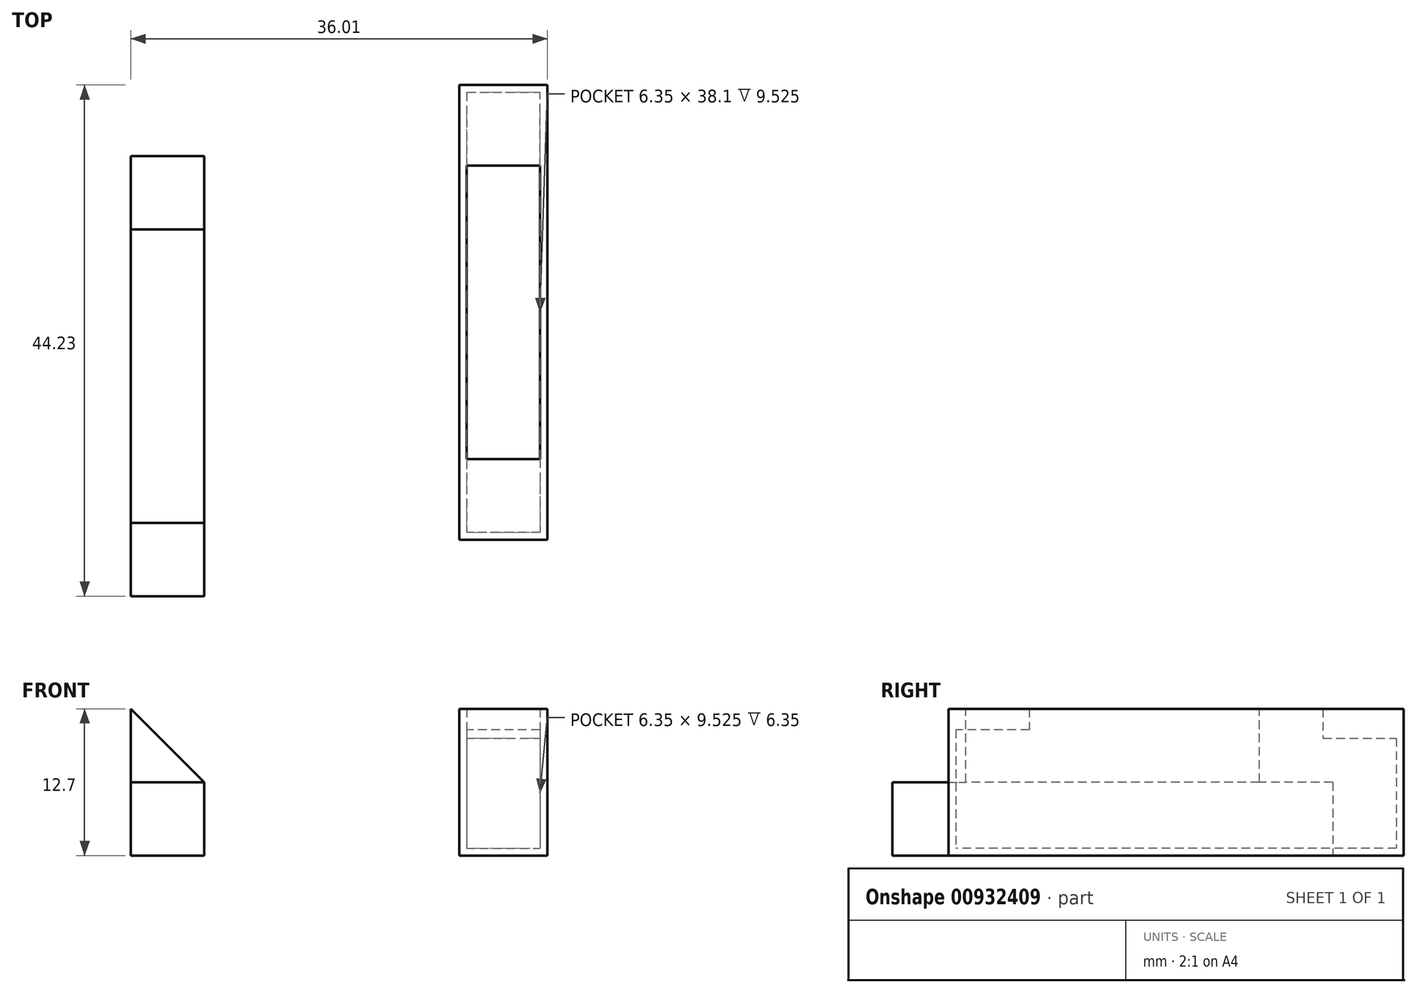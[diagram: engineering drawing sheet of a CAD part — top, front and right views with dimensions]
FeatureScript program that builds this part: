
annotation { "Feature Type Name" : "Feature", "Feature Type Description" : "" }
export const myFeature = defineFeature(function(context is Context, id is Id, definition is map)
    precondition{}
    {
        {
            var Q0;
            Q0=qCreatedBy(makeId("Top.planeOp"),FACE);
            var sketch = newSketch(context, id + "F0", { "sketchPlane" : qUnion([Q0])});
            skLineSegment(sketch, "E0.bottom", {"start": v(0, 0) * mm, "end": v(6.35, 0) * mm});
            skLineSegment(sketch, "E0.top", {"start": v(0, -25.4) * mm, "end": v(6.35, -25.4) * mm});
            skLineSegment(sketch, "E0.left", {"start": v(0, 0) * mm, "end": v(0, -25.4) * mm});
            skLineSegment(sketch, "E0.right", {"start": v(6.35, 0) * mm, "end": v(6.35, -25.4) * mm});
            skLineSegment(sketch, "E1.bottom", {"start": v(28.4, 12.48) * mm, "end": v(36.01, 12.48) * mm});
            skLineSegment(sketch, "E1.top", {"start": v(28.4, -26.89) * mm, "end": v(36.01, -26.89) * mm});
            skLineSegment(sketch, "E1.left", {"start": v(28.4, 12.48) * mm, "end": v(28.4, -26.89) * mm});
            skLineSegment(sketch, "E1.right", {"start": v(36.01, 12.48) * mm, "end": v(36.01, -26.89) * mm});
            skLineSegment(sketch, "E2.bottom", {"start": v(-49.7, 10.3) * mm, "end": v(-42.72, 10.3) * mm});
            skLineSegment(sketch, "E2.top", {"start": v(-49.7, -27.8) * mm, "end": v(-42.72, -27.8) * mm});
            skLineSegment(sketch, "E2.left", {"start": v(-49.7, 10.3) * mm, "end": v(-49.7, -27.8) * mm});
            skLineSegment(sketch, "E2.right", {"start": v(-42.72, 10.3) * mm, "end": v(-42.72, -27.8) * mm});
            skSolve(sketch);
        }
        {
            var Q0;
            Q0=makeQuery(id+"F0.imprint","IMPRINT",FACE,{"disambiguationData":[TD([[makeQuery(id+"F0.imprint","IMPRINT",EDGE,{"derivedFrom":sQuery(id+"F0.wireOp",EDGE,"E0.bottom")}),-1.0]])]});
            extrude(context, id + "F1", {"entities" : qUnion([Q0]), "depth" : 12.7 * mm, "offsetDistance" : 25 * mm});
        }
        {
            var Q0;
            Q0=makeQuery(id+"F1.opExtrude","SWEPT_FACE",FACE,{"disambiguationData":[OSD([sQuery(id+"F0.wireOp",EDGE,"E0.top")])]});
            var sketch = newSketch(context, id + "F2", { "sketchPlane" : qUnion([Q0])});
            skLineSegment(sketch, "E3", {"start": v(6.35, 6.35) * mm, "end": v(0, 12.7) * mm});
            skLineSegment(sketch, "E4", {"start": v(0, 12.7) * mm, "end": v(6.35, 12.7) * mm});
            skLineSegment(sketch, "E5", {"start": v(6.35, 12.7) * mm, "end": v(6.35, 6.35) * mm});
            skSolve(sketch);
        }
        {
            var Q0;
            Q0=makeQuery(id+"F2.imprint","IMPRINT",FACE,{"disambiguationData":[TD([[makeQuery(id+"F2.imprint","IMPRINT",EDGE,{"derivedFrom":sQuery(id+"F2.wireOp",EDGE,"E3")}),-1.0]])]});
            extrude(context, id + "F3", {"entities" : qUnion([Q0]), "operationType" : NewBodyOperationType.REMOVE, "endBound" : BoundingType.UP_TO_NEXT, "oppositeDirection" : true, "depth" : 25.4 * mm, "offsetDistance" : 25.4 * mm});
        }
        {
            var Q0;
            Q0=makeQuery(id+"F0.imprint","IMPRINT",FACE,{"disambiguationData":[TD([[makeQuery(id+"F0.imprint","IMPRINT",EDGE,{"derivedFrom":sQuery(id+"F0.wireOp",EDGE,"E1.bottom")}),-1.0]])]});
            extrude(context, id + "F4", {"entities" : qUnion([Q0]), "depth" : 12.7 * mm, "offsetDistance" : 25.4 * mm});
        }
        {
            var Q0;
            Q0=makeQuery(id+"F4.opExtrude","CAP_FACE",FACE,{"disambiguationData":[OSD([sQuery(id+"F0.wireOp",EDGE,"E1.bottom"),sQuery(id+"F0.wireOp",EDGE,"E1.top"),sQuery(id+"F0.wireOp",EDGE,"E1.left"),sQuery(id+"F0.wireOp",EDGE,"E1.right")])],"isStart":false});
            shell(context, id + "F5", {"entities" : qUnion([Q0]), "thickness" : 0.64 * mm});
        }
        {
            var Q0;
            Q0=makeQuery(id+"F1.opExtrude","SWEPT_FACE",FACE,{"disambiguationData":[OSD([sQuery(id+"F0.wireOp",EDGE,"E0.top")])]});
            var sketch = newSketch(context, id + "F6", { "sketchPlane" : qUnion([Q0])});
            skLineSegment(sketch, "E6", {"start": v(6.35, 6.35) * mm, "end": v(0, 6.35) * mm});
            skLineSegment(sketch, "E7", {"start": v(0, 6.35) * mm, "end": v(0, 0) * mm});
            skLineSegment(sketch, "E8", {"start": v(0, 0) * mm, "end": v(6.35, 0) * mm});
            skLineSegment(sketch, "E9", {"start": v(6.35, 0) * mm, "end": v(6.35, 6.35) * mm});
            skSolve(sketch);
        }
        {
            var Q0;
            Q0=makeQuery(id+"F6.imprint","IMPRINT",FACE,{"disambiguationData":[TD([[makeQuery(id+"F6.imprint","IMPRINT",EDGE,{"derivedFrom":sQuery(id+"F6.wireOp",EDGE,"E6")}),1.0]])]});
            extrude(context, id + "F7", {"entities" : qUnion([Q0]), "operationType" : NewBodyOperationType.ADD, "depth" : 6.35 * mm, "offsetDistance" : 25.4 * mm});
        }
        {
            var Q0;
            Q0=makeQuery(id+"F1.opExtrude","SWEPT_FACE",FACE,{"disambiguationData":[OSD([sQuery(id+"F0.wireOp",EDGE,"E0.bottom")])]});
            var sketch = newSketch(context, id + "F8", { "sketchPlane" : qUnion([Q0])});
            skLineSegment(sketch, "E10", {"start": v(-6.35, 6.35) * mm, "end": v(0, 6.35) * mm});
            skLineSegment(sketch, "E11", {"start": v(0, 6.35) * mm, "end": v(0, 0) * mm});
            skLineSegment(sketch, "E12", {"start": v(0, 0) * mm, "end": v(-6.35, 0) * mm});
            skLineSegment(sketch, "E13", {"start": v(-6.35, 0) * mm, "end": v(-6.35, 6.35) * mm});
            skSolve(sketch);
        }
        {
            var Q0;
            Q0=makeQuery(id+"F8.imprint","IMPRINT",FACE,{"disambiguationData":[TD([[makeQuery(id+"F8.imprint","IMPRINT",EDGE,{"derivedFrom":sQuery(id+"F8.wireOp",EDGE,"E10")}),-1.0]])]});
            extrude(context, id + "F9", {"entities" : qUnion([Q0]), "operationType" : NewBodyOperationType.ADD, "depth" : 6.35 * mm, "offsetDistance" : 25.4 * mm});
        }
        {
            var Q0;
            Q0=makeQuery(id+"F5.opShell","OFFSET_FACE",FACE,{"disambiguationData":[OSD([sQuery(id+"F0.wireOp",EDGE,"E1.bottom")])]});
            var sketch = newSketch(context, id + "F10", { "sketchPlane" : qUnion([Q0])});
            skLineSegment(sketch, "E14", {"start": v(29.03, 10.16) * mm, "end": v(35.38, 10.16) * mm});
            skLineSegment(sketch, "E15", {"start": v(35.38, 10.16) * mm, "end": v(35.38, 12.7) * mm});
            skLineSegment(sketch, "E16", {"start": v(35.38, 12.7) * mm, "end": v(29.03, 12.7) * mm});
            skLineSegment(sketch, "E17", {"start": v(29.03, 12.7) * mm, "end": v(29.03, 10.16) * mm});
            skSolve(sketch);
        }
        {
            var Q0;
            Q0=makeQuery(id+"F10.imprint","IMPRINT",FACE,{"disambiguationData":[TD([[makeQuery(id+"F10.imprint","IMPRINT",EDGE,{"derivedFrom":sQuery(id+"F10.wireOp",EDGE,"E14")}),1.0]])]});
            extrude(context, id + "F11", {"entities" : qUnion([Q0]), "operationType" : NewBodyOperationType.ADD, "depth" : 6.35 * mm, "offsetDistance" : 25.4 * mm});
        }
        {
            var Q0;
            Q0=makeQuery(id+"F5.opShell","OFFSET_FACE",FACE,{"disambiguationData":[OSD([sQuery(id+"F0.wireOp",EDGE,"E1.top")])]});
            var sketch = newSketch(context, id + "F12", { "sketchPlane" : qUnion([Q0])});
            skLineSegment(sketch, "E18", {"start": v(-35.38, 10.9) * mm, "end": v(-29.03, 10.9) * mm});
            skLineSegment(sketch, "E19", {"start": v(-29.03, 10.9) * mm, "end": v(-29.03, 12.7) * mm});
            skLineSegment(sketch, "E20", {"start": v(-29.03, 12.7) * mm, "end": v(-35.38, 12.7) * mm});
            skLineSegment(sketch, "E21", {"start": v(-35.38, 12.7) * mm, "end": v(-35.38, 10.9) * mm});
            skSolve(sketch);
        }
        {
            var Q0;
            Q0=makeQuery(id+"F12.imprint","IMPRINT",FACE,{"disambiguationData":[TD([[makeQuery(id+"F12.imprint","IMPRINT",EDGE,{"derivedFrom":sQuery(id+"F12.wireOp",EDGE,"E18")}),1.0]])]});
            extrude(context, id + "F13", {"entities" : qUnion([Q0]), "operationType" : NewBodyOperationType.ADD, "depth" : 6.35 * mm, "offsetDistance" : 25.4 * mm});
        }
    });
